# Revit family: ASH_Contour21_S6466_BIM_GB
name_source: partatom
category: Plumbing Fixtures
revit_build: Autodesk Revit MEP 2012 (Build: 20110309_2315(x64)
units: mm (PartAtom-declared; Revit-internal decimal feet)

## types (5) — shared parameters
AccessibilityPerformance = DDA Compliant
Accessories = www.idealspec.co.uk
Assembly Code = C1030200
AssetType = Fixed
BIMObjectName = GRABRAIL_ArmitageShanks_Contour21-BackRestfor75cmPan_S6466
BREEAM Approved = No
Brand = Armitage Shanks
Category = Furniture_GRABRAIL_UK
ConnectionType = Mechanical
CurrentRevision = 1
Default Elevation = 1219 mm
Description = Contour 21 back support rail for 75cm projection WC, 40 x 22 x 35mm diameter tube
DurationUnit = Years
ECA = No
ElementType = GRAB RAIL: Safety device to aid maintaining balance, lessen fatigue and assist in supporting weight whilst maneuvering the body
ExpectedLife = 30
Help = http://www.idealspec.co.uk
InstallationInstructions = http://www.idealspec.co.uk
Manufacturer = Ideal Standard International Ltd
ManufacturerURL = www.idealspec.co.uk
Name = GRABRAIL_ArmitageShanks_Contour21-BackRestfor75cmPan_S6466
NettWeight = 4.62Kg (inc.cushion)
NominalHeight = 220 mm  [stored 0.721785 ft]
NominalLength = 400 mm  [stored 1.31234 ft]
NominalWidth = 84 mm
PredefinedType = grabrail
ProductDataSheet = http://www.idealspec.co.uk
ProductInformation = http://www.idealspec.co.uk
S6884AC Cushion = Yes
SalesInformation = http://www.idealspec.co.uk
SendEnquiry = http://www.idealspec.co.uk
Shape = Tubular
Size = 400mm x 220mm x 84mm
Space = Internal
SpareParts = www.fastpart-spares.co.uk
StandardsConformance = DDA, Doc-M
URL = www.idealspec.co.uk
Version = 2
VolumeUnits = Litres
WRAS = No
WarrantyDescription = Manufacturers Warranty
WarrantyDurationParts = 5
WarrantyDurationUnit = Years
WarrantyGuarantorParts = Ideal Standard International Ltd
WaterEfficientProduct = No

## per-type parameters (varying)
| type | Colour | Features | Finish | Grade | LRVValue | Material | Model | ModelNumber | ModelReference | RAL |
| S6466LI | Powder Coated Aluminium Blue LI | 40 x 22 x 35mm diameter tube Blue | Powder Coated Aluminium Blue LI | T6 | 27 | Aluminium | S646636 | S646636 | S646636 | 5011 |
| S646601 | Powder Coated Aluminium White 01 | 40 x 22 x 35mm diameter tube White | Powder Coated Aluminium White 01 | T6 | 94 | Alumnium | S6466AC | S6466AC | S6466AC | 9016 |
| S6466LJ | Powder Coated Aluminium Grey LJ | 40 x 22 x 35mm diameter tube Light Grey | Powder Coated Aluminium Grey LJ | T6 | 20 | Aluminium | S6466LJ | S6466LJ | S6466LJ | 7005 |
| S6466RN | Powder Coated Aluminium Charcoal RN | 40 x 22 x 35mm diameter tube Charcoal | Powder Coated Aluminium Charcoal RN | T6 | 9 | Aluminium | S6466RN | S6466RN | S6466RN | 7016 |
| S6466MY | Stainless Steel MY | 40 x 22 x 35mm diameter tube Stainless Steel | Polished | 304 |  | Stainless Steel | S6466MY | S6466MY | S6466MY |  |

note: column(s) folded — value = type name in every type: PartNumber

note: [stored X ft] marks values corroborated as IEEE doubles in the binary element streams (Revit-internal decimal feet)

## geometry (parser evidence)
native form markers: Blend x5, Sweep x3
no freeform markers — native parametric forms only
